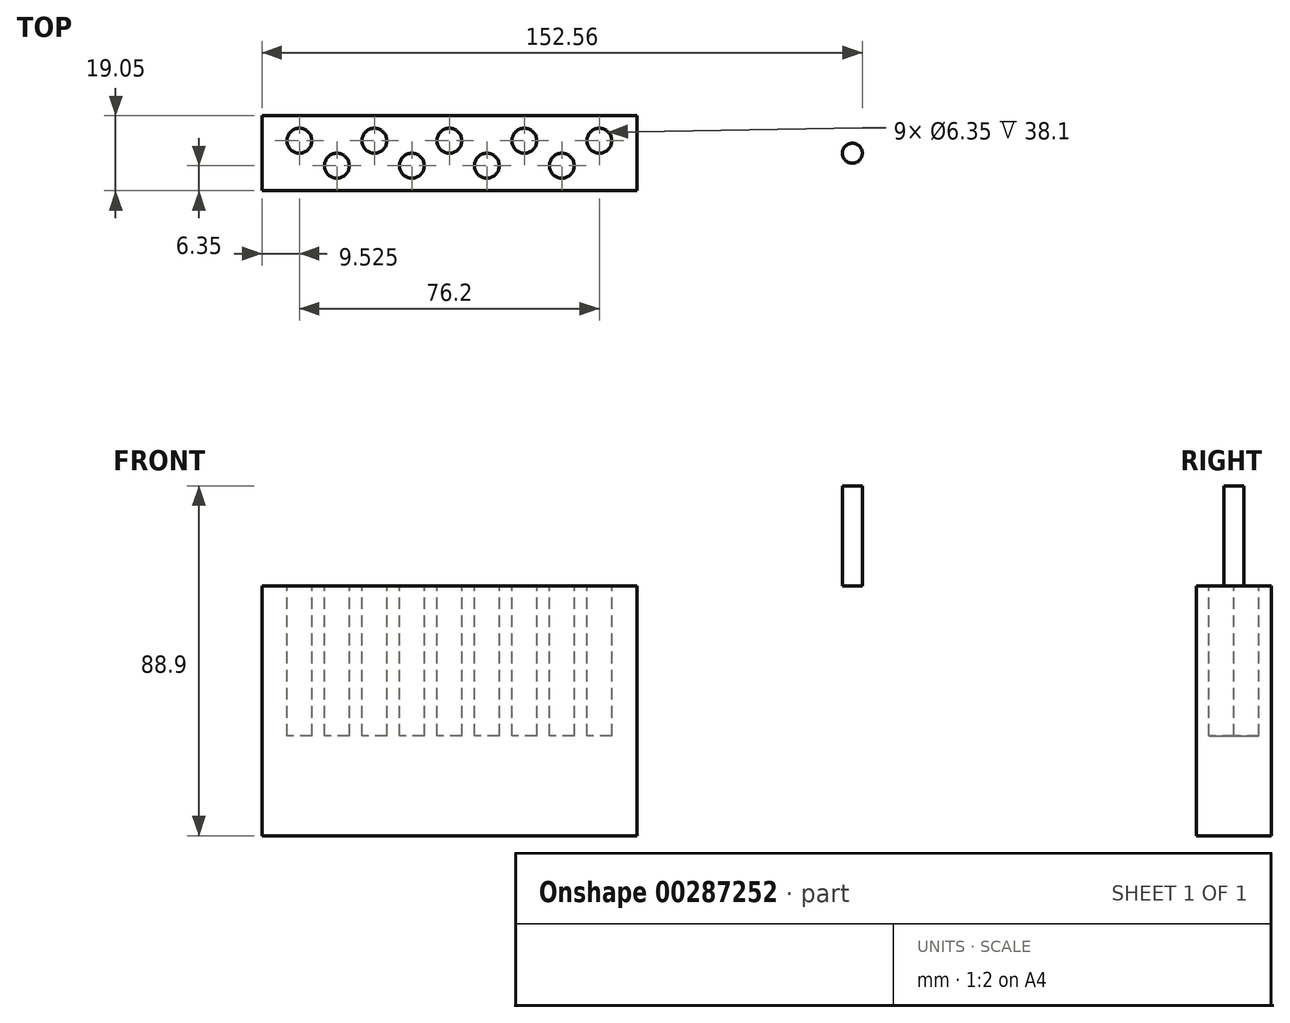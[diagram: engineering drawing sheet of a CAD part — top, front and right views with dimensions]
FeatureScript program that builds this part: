
annotation { "Feature Type Name" : "Feature", "Feature Type Description" : "" }
export const myFeature = defineFeature(function(context is Context, id is Id, definition is map)
    precondition{}
    {
        {
            var Q0;
            Q0=qCreatedBy(makeId("Top.planeOp"),FACE);
            var sketch = newSketch(context, id + "F0", { "sketchPlane" : qUnion([Q0])});
            skLineSegment(sketch, "E0.bottom", {"start": v(0, 0) * mm, "end": v(95.25, 0) * mm});
            skLineSegment(sketch, "E0.top", {"start": v(0, 19.05) * mm, "end": v(95.25, 19.05) * mm});
            skLineSegment(sketch, "E0.left", {"start": v(0, 0) * mm, "end": v(0, 19.05) * mm});
            skLineSegment(sketch, "E0.right", {"start": v(95.25, 0) * mm, "end": v(95.25, 19.05) * mm});
            skSolve(sketch);
        }
        {
            var Q0;
            Q0 = qSketchRegion(id + "F0", true);
            extrude(context, id + "F1", {"entities" : qUnion([Q0]), "oppositeDirection" : true, "depth" : 63.5 * mm});
        }
        {
            var Q0;
            Q0=qCreatedBy(makeId("Top.planeOp"),FACE);
            var sketch = newSketch(context, id + "F2", { "sketchPlane" : qUnion([Q0])});
            skCircle(sketch, "E1", {"center": v(9.53, 12.7) * mm, "radius": 3.18 * mm});
            skCircle(sketch, "E2.1.0.0", {"center": v(28.58, 12.7) * mm, "radius": 3.18 * mm});
            skCircle(sketch, "E2.2.0.0", {"center": v(47.63, 12.7) * mm, "radius": 3.18 * mm});
            skCircle(sketch, "E2.3.0.0", {"center": v(66.68, 12.7) * mm, "radius": 3.18 * mm});
            skCircle(sketch, "E2.4.0.0", {"center": v(85.73, 12.7) * mm, "radius": 3.18 * mm});
            skLineSegment(sketch, "E2.direction1", {"start": v(9.53, 12.7) * mm, "end": v(28.58, 12.7) * mm, "construction": true});
            skCircle(sketch, "E3", {"center": v(19.05, 6.35) * mm, "radius": 3.18 * mm});
            skCircle(sketch, "E4.1.0.0", {"center": v(38.1, 6.35) * mm, "radius": 3.18 * mm});
            skCircle(sketch, "E4.2.0.0", {"center": v(57.15, 6.35) * mm, "radius": 3.18 * mm});
            skCircle(sketch, "E4.3.0.0", {"center": v(76.2, 6.35) * mm, "radius": 3.18 * mm});
            skLineSegment(sketch, "E4.direction1", {"start": v(19.05, 6.35) * mm, "end": v(38.1, 6.35) * mm, "construction": true});
            skSolve(sketch);
        }
        {
            var Q0;
            Q0 = qSketchRegion(id + "F2", true);
            extrude(context, id + "F3", {"entities" : qUnion([Q0]), "operationType" : NewBodyOperationType.REMOVE, "depth" : 38.1 * mm});
        }
        {
            var Q0;
            Q0 = qSketchRegion(id + "F2", true);
            extrude(context, id + "F4", {"entities" : qUnion([Q0]), "operationType" : NewBodyOperationType.REMOVE, "oppositeDirection" : true, "depth" : 38.1 * mm});
        }
        {
            var Q0;
            Q0=qCreatedBy(makeId("Top.planeOp"),FACE);
            var sketch = newSketch(context, id + "F5", { "sketchPlane" : qUnion([Q0])});
            skCircle(sketch, "E5.2.0.0", {"center": v(150.02, 9.52) * mm, "radius": 2.54 * mm});
            skLineSegment(sketch, "E5.direction1", {"start": v(13.5, 9.52) * mm, "end": v(81.76, 9.52) * mm, "construction": true});
            skSolve(sketch);
        }
        {
            var Q0;
            Q0 = qSketchRegion(id + "F5", true);
            extrude(context, id + "F6", {"entities" : qUnion([Q0]), "depth" : 25.4 * mm});
        }
    });
